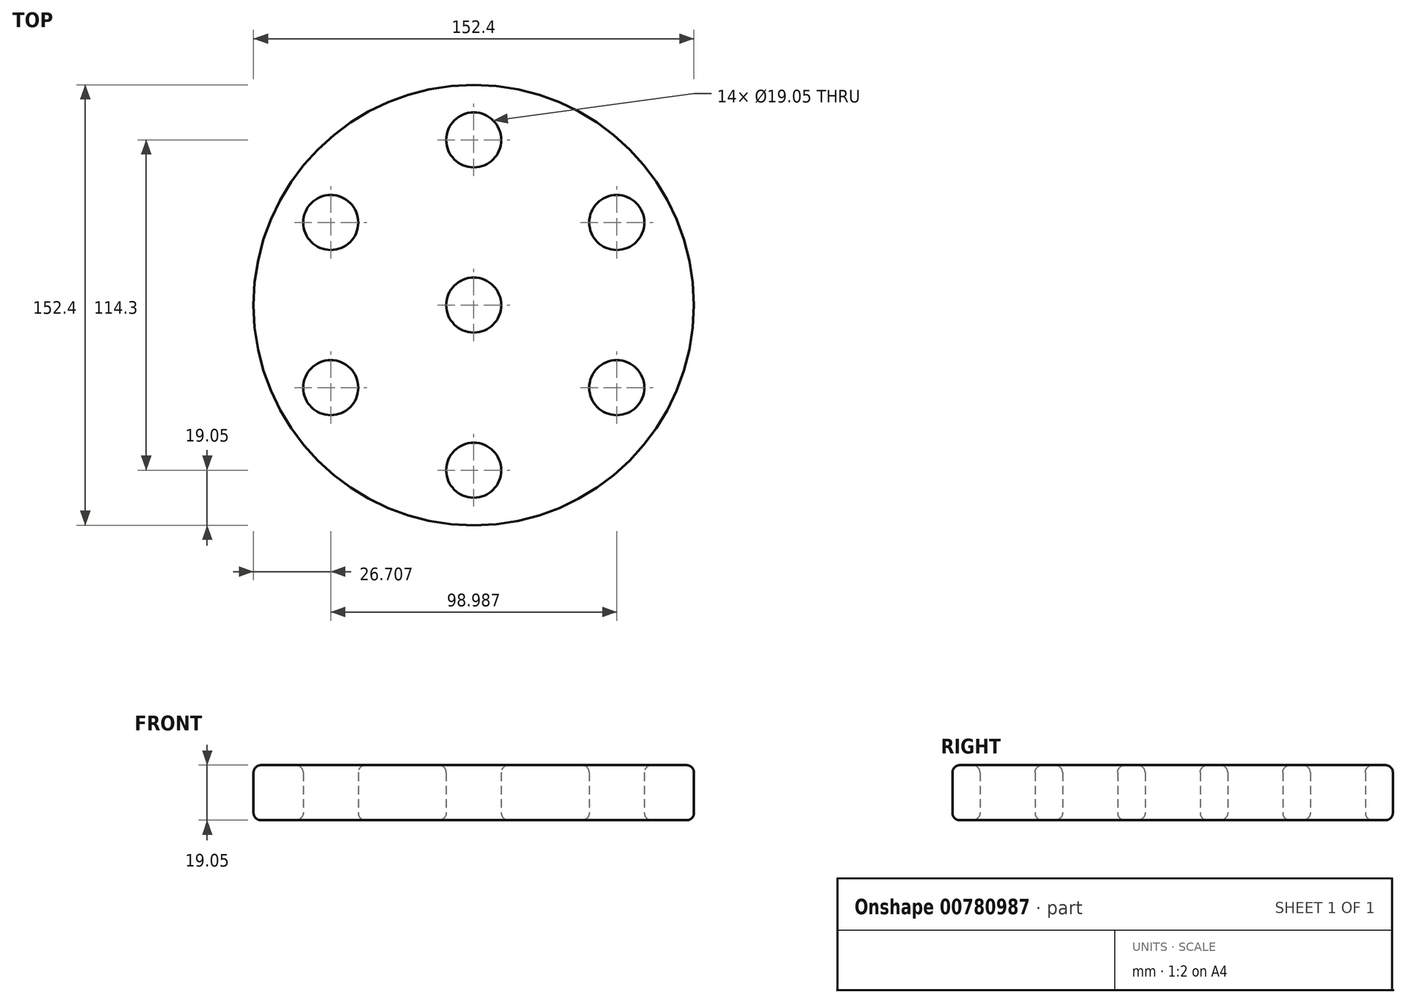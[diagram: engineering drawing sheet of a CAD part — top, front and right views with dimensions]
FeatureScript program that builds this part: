
annotation { "Feature Type Name" : "Feature", "Feature Type Description" : "" }
export const myFeature = defineFeature(function(context is Context, id is Id, definition is map)
    precondition{}
    {
        {
            var Q0;
            Q0=qCreatedBy(makeId("Top.planeOp"),FACE);
            var sketch = newSketch(context, id + "F0", { "sketchPlane" : qUnion([Q0])});
            skCircle(sketch, "E0", {"center": v(0, 0) * mm, "radius": 76.2 * mm});
            skCircle(sketch, "E1", {"center": v(0, 57.15) * mm, "radius": 9.53 * mm});
            skCircle(sketch, "E2.1.0", {"center": v(-49.5, 28.58) * mm, "radius": 9.53 * mm});
            skCircle(sketch, "E2.2.0", {"center": v(-49.5, -28.57) * mm, "radius": 9.53 * mm});
            skCircle(sketch, "E2.3.0", {"center": v(0, -57.15) * mm, "radius": 9.53 * mm});
            skCircle(sketch, "E2.4.0", {"center": v(49.5, -28.58) * mm, "radius": 9.53 * mm});
            skCircle(sketch, "E2.5.0", {"center": v(49.5, 28.58) * mm, "radius": 9.53 * mm});
            skCircle(sketch, "E3", {"center": v(0, 0) * mm, "radius": 9.53 * mm});
            skSolve(sketch);
        }
        {
            var Q0;
            Q0=makeQuery(id+"F0.imprint","IMPRINT",FACE,{"disambiguationData":[TD([[makeQuery(id+"F0.imprint","IMPRINT",EDGE,{"derivedFrom":sQuery(id+"F0.wireOp",EDGE,"E0")}),1.0]])]});
            extrude(context, id + "F1", {"entities" : qUnion([Q0]), "depth" : 19.05 * mm, "offsetDistance" : 25.4 * mm});
        }
        {
            var Q0;
            Q0=makeQuery(id+"F1.opExtrude","CAP_EDGE",EDGE,{"disambiguationData":[OSD([sQuery(id+"F0.wireOp",EDGE,"E2.1.0")])],"isStart":false});
            var Q1;
            Q1=makeQuery(id+"F1.opExtrude","CAP_EDGE",EDGE,{"disambiguationData":[OSD([sQuery(id+"F0.wireOp",EDGE,"E1")])],"isStart":false});
            var Q2;
            Q2=makeQuery(id+"F1.opExtrude","CAP_EDGE",EDGE,{"disambiguationData":[OSD([sQuery(id+"F0.wireOp",EDGE,"E2.5.0")])],"isStart":false});
            var Q3;
            Q3=makeQuery(id+"F1.opExtrude","CAP_EDGE",EDGE,{"disambiguationData":[OSD([sQuery(id+"F0.wireOp",EDGE,"E2.4.0")])],"isStart":false});
            var Q4;
            Q4=makeQuery(id+"F1.opExtrude","CAP_EDGE",EDGE,{"disambiguationData":[OSD([sQuery(id+"F0.wireOp",EDGE,"E2.3.0")])],"isStart":false});
            var Q5;
            Q5=makeQuery(id+"F1.opExtrude","CAP_EDGE",EDGE,{"disambiguationData":[OSD([sQuery(id+"F0.wireOp",EDGE,"E2.2.0")])],"isStart":false});
            var Q6;
            Q6=makeQuery(id+"F1.opExtrude","CAP_EDGE",EDGE,{"disambiguationData":[OSD([sQuery(id+"F0.wireOp",EDGE,"E3")])],"isStart":false});
            var Q7;
            Q7=makeQuery(id+"F1.opExtrude","CAP_EDGE",EDGE,{"disambiguationData":[OSD([sQuery(id+"F0.wireOp",EDGE,"E2.1.0")])],"isStart":true});
            var Q8;
            Q8=makeQuery(id+"F1.opExtrude","CAP_EDGE",EDGE,{"disambiguationData":[OSD([sQuery(id+"F0.wireOp",EDGE,"E2.2.0")])],"isStart":true});
            var Q9;
            Q9=makeQuery(id+"F1.opExtrude","CAP_EDGE",EDGE,{"disambiguationData":[OSD([sQuery(id+"F0.wireOp",EDGE,"E3")])],"isStart":true});
            var Q10;
            Q10=makeQuery(id+"F1.opExtrude","CAP_EDGE",EDGE,{"disambiguationData":[OSD([sQuery(id+"F0.wireOp",EDGE,"E1")])],"isStart":true});
            var Q11;
            Q11=makeQuery(id+"F1.opExtrude","CAP_EDGE",EDGE,{"disambiguationData":[OSD([sQuery(id+"F0.wireOp",EDGE,"E2.5.0")])],"isStart":true});
            var Q12;
            Q12=makeQuery(id+"F1.opExtrude","CAP_EDGE",EDGE,{"disambiguationData":[OSD([sQuery(id+"F0.wireOp",EDGE,"E2.4.0")])],"isStart":true});
            var Q13;
            Q13=makeQuery(id+"F1.opExtrude","CAP_EDGE",EDGE,{"disambiguationData":[OSD([sQuery(id+"F0.wireOp",EDGE,"E2.3.0")])],"isStart":true});
            fillet(context, id + "F2", {"entities" : qUnion([Q0, Q1, Q2, Q3, Q4, Q5, Q6, Q7, Q8, Q9, Q10, Q11, Q12, Q13]), "radius" : 2.54 * mm, "tangentPropagation" : true, "allowEdgeOverflow" : false});
        }
        {
            var Q0;
            Q0=makeQuery(id+"F1.opExtrude","CAP_EDGE",EDGE,{"disambiguationData":[OSD([sQuery(id+"F0.wireOp",EDGE,"E0")])],"isStart":true});
            var Q1;
            Q1=makeQuery(id+"F1.opExtrude","CAP_EDGE",EDGE,{"disambiguationData":[OSD([sQuery(id+"F0.wireOp",EDGE,"E0")])],"isStart":false});
            fillet(context, id + "F3", {"entities" : qUnion([Q0, Q1]), "radius" : 2.54 * mm, "tangentPropagation" : true, "allowEdgeOverflow" : false});
        }
    });
